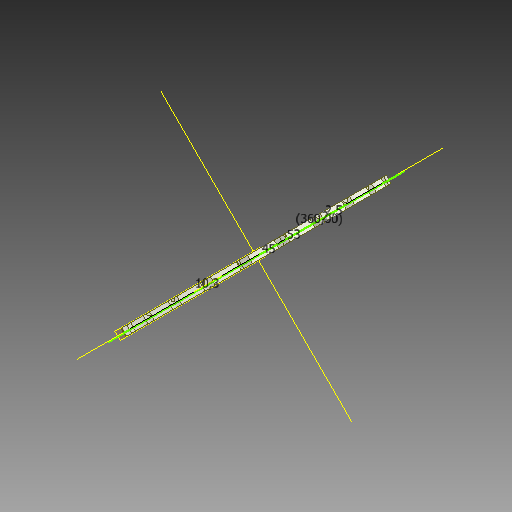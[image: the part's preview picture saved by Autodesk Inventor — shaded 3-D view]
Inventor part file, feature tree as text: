
AUTODESK INVENTOR PART (.ipt)
format: ipt  version: 2020 (Build 240168000, 168)  size: 494,080 bytes
history: native  units: mm
features: other x4, sketch x4, extrude x2, revolve x2, pattern_circular x1
ambient origin geometry x8: Origin, YZ Plane, XZ Plane, XY Plane, X Axis, Y Axis, Z Axis, Center Point
bodies: Body1 (feature_tree)
feature tree (13):
  other  "РабПлоскость2"
  sketch  "Эскиз1"
  extrude  "Выдавливание1"  Depth=45.0mm
  revolve  "Вращение2"
  pattern_circular  "Круговой массив1"  [2 undecoded]
  other  "РабПлоскость3"
  sketch  "Эскиз3"
  other  "РабОсь3"
  revolve  "Вращение4"
  extrude  "Выдавливание3"  Depth=2.0mm
  sketch  "Эскиз5"
  sketch  "Эскиз4"
  other  "Твердое тело1"
note: 2 required parameter values undecoded (feature->parameter linkage not recoverable at this tier; creation-order binding heuristic only, values carry confidence <= 0.55)
